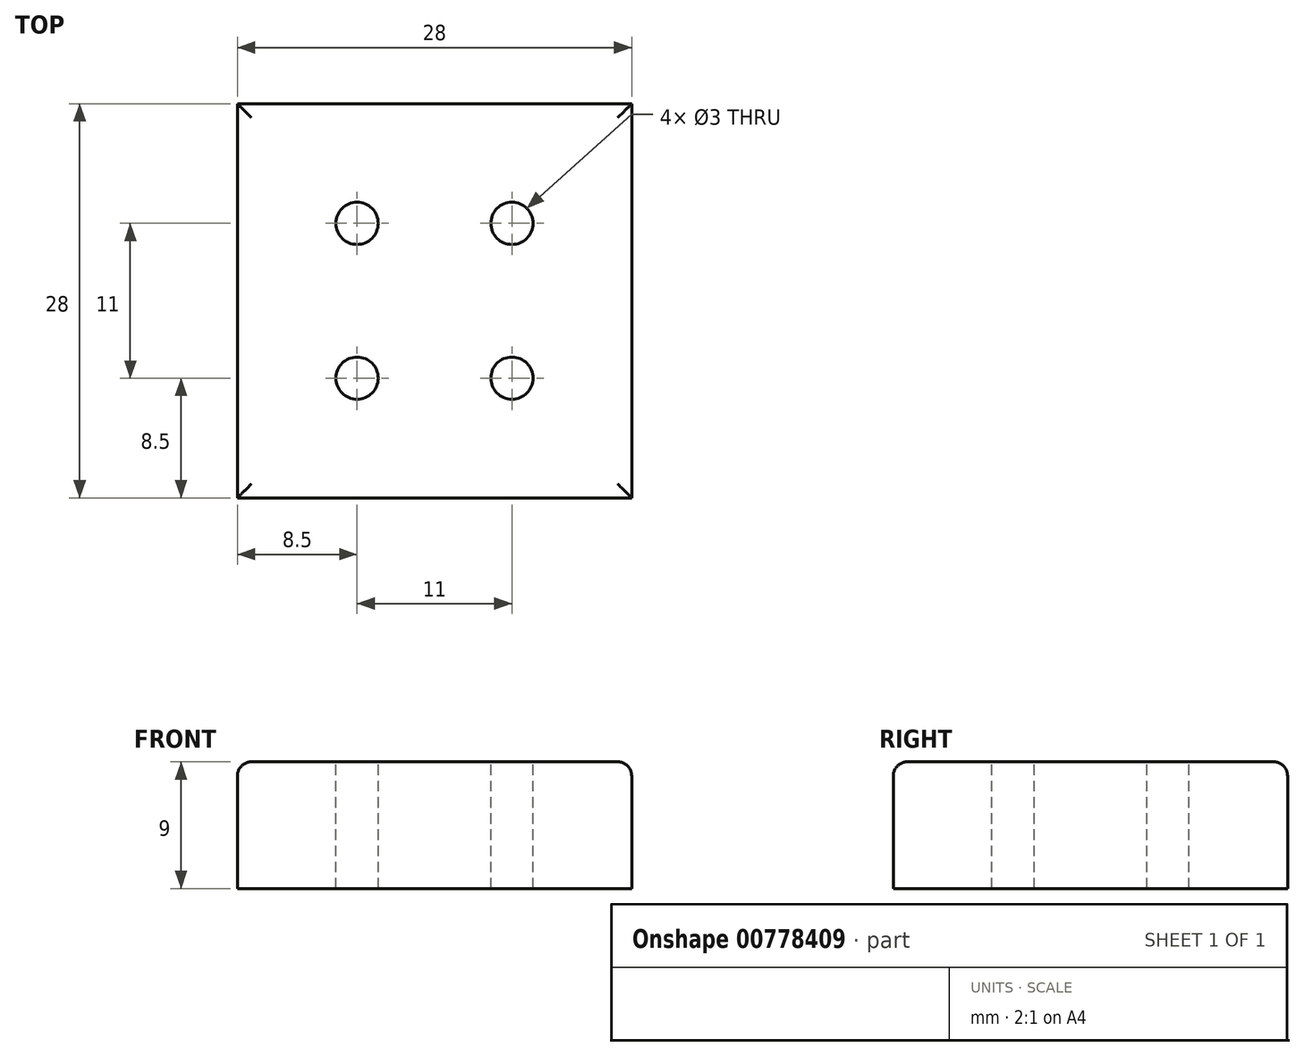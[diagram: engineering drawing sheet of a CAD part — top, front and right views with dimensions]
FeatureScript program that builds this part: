
annotation { "Feature Type Name" : "Feature", "Feature Type Description" : "" }
export const myFeature = defineFeature(function(context is Context, id is Id, definition is map)
    precondition{}
    {
        {
            var Q0;
            Q0=qCreatedBy(makeId("Top.planeOp"),FACE);
            var sketch = newSketch(context, id + "F0", { "sketchPlane" : qUnion([Q0])});
            skLineSegment(sketch, "E0.bottom", {"start": v(14, -14) * mm, "end": v(-14, -14) * mm});
            skLineSegment(sketch, "E0.top", {"start": v(14, 14) * mm, "end": v(-14, 14) * mm});
            skLineSegment(sketch, "E0.left", {"start": v(14, -14) * mm, "end": v(14, 14) * mm});
            skLineSegment(sketch, "E0.right", {"start": v(-14, -14) * mm, "end": v(-14, 14) * mm});
            skPoint(sketch, "E0.middle", {"position": v(0, 0) * mm});
            skSolve(sketch);
        }
        {
            var Q0;
            Q0 = qSketchRegion(id + "F0", true);
            extrude(context, id + "F1", {"entities" : qUnion([Q0]), "depth" : 9 * mm, "offsetDistance" : 25 * mm});
        }
        {
            var Q0;
            Q0=makeQuery(id+"F1.opExtrude","CAP_FACE",FACE,{"disambiguationData":[OSD([sQuery(id+"F0.wireOp",EDGE,"E0.bottom"),sQuery(id+"F0.wireOp",EDGE,"E0.top"),sQuery(id+"F0.wireOp",EDGE,"E0.left"),sQuery(id+"F0.wireOp",EDGE,"E0.right")])],"isStart":false});
            var sketch = newSketch(context, id + "F2", { "sketchPlane" : qUnion([Q0])});
            skPoint(sketch, "E1", {"position": v(5.5, 5.5) * mm});
            skLineSegment(sketch, "E2.bottom", {"start": v(5.5, 5.5) * mm, "end": v(-5.5, 5.5) * mm});
            skLineSegment(sketch, "E2.top", {"start": v(5.5, -5.5) * mm, "end": v(-5.5, -5.5) * mm});
            skLineSegment(sketch, "E2.left", {"start": v(5.5, 5.5) * mm, "end": v(5.5, -5.5) * mm});
            skLineSegment(sketch, "E2.right", {"start": v(-5.5, 5.5) * mm, "end": v(-5.5, -5.5) * mm});
            skSolve(sketch);
        }
        {
            var Q0;
            Q0=sQuery(id+"F2.wireOp",VERTEX,"qznFlWvu-ZYcL-xSM1-zkij-XPYoCRPUi4VT.top.end");
            var Q1;
            Q1=sQuery(id+"F2.wireOp",VERTEX,"qznFlWvu-ZYcL-xSM1-zkij-XPYoCRPUi4VT.bottom.end");
            var Q2;
            Q2=sQuery(id+"F2.wireOp",VERTEX,"qznFlWvu-ZYcL-xSM1-zkij-XPYoCRPUi4VT.bottom.start");
            var Q3;
            Q3=sQuery(id+"F2.wireOp",VERTEX,"qznFlWvu-ZYcL-xSM1-zkij-XPYoCRPUi4VT.top.start");
            var Q4;
            Q4=sQuery(id+"F2.wireOp",VERTEX,"E1");
            var Q5;
            Q5=sQuery(id+"F2.wireOp",VERTEX,"E2.bottom.end");
            var Q6;
            Q6=sQuery(id+"F2.wireOp",VERTEX,"E2.top.end");
            var Q7;
            Q7=sQuery(id+"F2.wireOp",VERTEX,"E2.top.start");
            var Q8;
            Q8=makeQuery(id+"F1.opExtrude","SWEPT_BODY",BODY,{"disambiguationData":[OSD([sQuery(id+"F0.wireOp",EDGE,"E0.bottom"),sQuery(id+"F0.wireOp",EDGE,"E0.top"),sQuery(id+"F0.wireOp",EDGE,"E0.left"),sQuery(id+"F0.wireOp",EDGE,"E0.right")])]});
            hole(context, id + "F3", {"style" : HoleStyle.SIMPLE, "endStyle" : HoleEndStyle.THROUGH, "holeDiameter" : 3 * mm, "majorDiameter" : 5 * mm, "isTappedThrough" : true, "tappedDepth" : 12 * mm, "tapClearance" : 3, "locations" : qUnion([Q0, Q1, Q2, Q3, Q4, Q5, Q6, Q7]), "scope" : qUnion([Q8])});
        }
        {
            var Q0;
            Q0=makeQuery(id+"F1.opExtrude","CAP_EDGE",EDGE,{"disambiguationData":[OSD([sQuery(id+"F0.wireOp",EDGE,"E0.top")])],"isStart":false});
            var Q1;
            Q1=makeQuery(id+"F1.opExtrude","CAP_EDGE",EDGE,{"disambiguationData":[OSD([sQuery(id+"F0.wireOp",EDGE,"E0.right")])],"isStart":false});
            var Q2;
            Q2=makeQuery(id+"F1.opExtrude","CAP_EDGE",EDGE,{"disambiguationData":[OSD([sQuery(id+"F0.wireOp",EDGE,"E0.bottom")])],"isStart":false});
            var Q3;
            Q3=makeQuery(id+"F1.opExtrude","CAP_EDGE",EDGE,{"disambiguationData":[OSD([sQuery(id+"F0.wireOp",EDGE,"E0.left")])],"isStart":false});
            fillet(context, id + "F4", {"entities" : qUnion([Q0, Q1, Q2, Q3]), "radius" : 1 * mm, "tangentPropagation" : true, "allowEdgeOverflow" : false});
        }
    });
